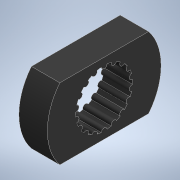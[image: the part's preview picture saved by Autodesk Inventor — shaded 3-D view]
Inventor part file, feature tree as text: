
AUTODESK INVENTOR PART (.ipt)
format: ipt  version: 2021 (Build 250183000, 183)  size: 150,528 bytes
history: native  units: mm
features: extrude x2, sketch x2
ambient origin geometry x8: Origin, YZ Plane, XZ Plane, XY Plane, X Axis, Y Axis, Z Axis, Center Point
bodies: Solid1 (feature_tree)
feature tree (4):
  extrude  "Extrusion1"  Depth=20.0mm
  extrude  "Extrusion2"  Depth=10.0mm
  sketch  "Sketch1"  dims[d0=20.0mm d1=40.0mm]
  sketch  "Sketch2"  dims[d4=10.0mm d5=0.0mm d6=2.0mm d7=180.0mm d9=360.0deg d11=10.0mm d12=0.0mm]
